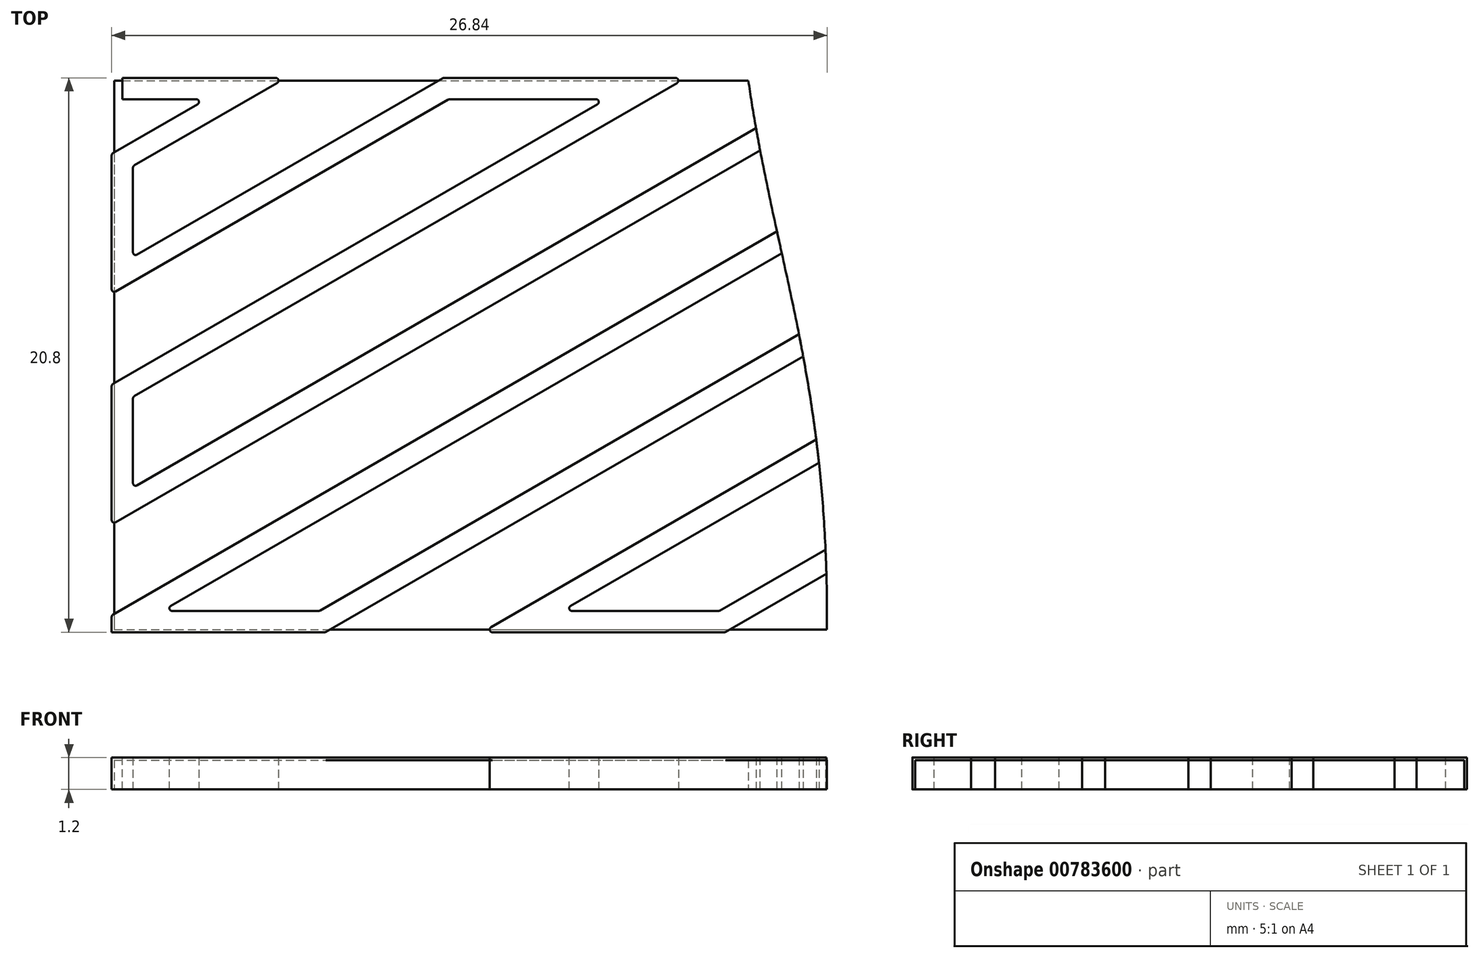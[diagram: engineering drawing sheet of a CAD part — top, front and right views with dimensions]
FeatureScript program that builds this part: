
annotation { "Feature Type Name" : "Feature", "Feature Type Description" : "" }
export const myFeature = defineFeature(function(context is Context, id is Id, definition is map)
    precondition{}
    {
        {
            var Q0;
            Q0=qCreatedBy(makeId("Top.planeOp"),FACE);
            var sketch = newSketch(context, id + "F0", { "sketchPlane" : qUnion([Q0])});
            skLineSegment(sketch, "E0.bottom", {"start": v(0, 0) * mm, "end": v(50, 0) * mm});
            skLineSegment(sketch, "E0.top", {"start": v(0, 20) * mm, "end": v(50, 20) * mm});
            skLineSegment(sketch, "E0.left", {"start": v(0, 0) * mm, "end": v(0, 20) * mm});
            skLineSegment(sketch, "E0.right", {"start": v(50, 0) * mm, "end": v(50, 20) * mm});
            skLineSegment(sketch, "E1", {"start": v(25, 36.98) * mm, "end": v(25, -17.72) * mm, "construction": true});
            skPoint(sketch, "E1.startSnap0", {"position": v(25, 20) * mm});
            skSolve(sketch);
        }
        {
            var Q0;
            Q0=sQuery(id+"F0.wireOp",EDGE,"E1");
            cPlane(context, id + "F1", {"entities" : qUnion([Q0]), "cplaneType" : CPlaneType.LINE_ANGLE, "offset" : 25 * mm, "angle" : 90 * degree, "width" : 150 * mm, "height" : 150 * mm});
        }
        {
            var Q0;
            Q0=qCreatedBy(makeId("Top.planeOp"),FACE);
            var sketch = newSketch(context, id + "F2", { "sketchPlane" : qUnion([Q0])});
            skLineSegment(sketch, "E2", {"start": v(0, 0) * mm, "end": v(34.64, 20) * mm});
            skLineSegment(sketch, "E3.1.0.0", {"start": v(7.5, 0) * mm, "end": v(42.14, 20) * mm});
            skLineSegment(sketch, "E3.2.0.0", {"start": v(15, 0) * mm, "end": v(49.64, 20) * mm});
            skLineSegment(sketch, "E3.3.0.0", {"start": v(22.5, 0) * mm, "end": v(50, 15.88) * mm});
            skLineSegment(sketch, "E3.4.0.0", {"start": v(30, 0) * mm, "end": v(50, 11.55) * mm});
            skLineSegment(sketch, "E3.5.0.0", {"start": v(37.5, 0) * mm, "end": v(50, 7.22) * mm});
            skLineSegment(sketch, "E3.6.0.0", {"start": v(45, 0) * mm, "end": v(50, 2.89) * mm});
            skLineSegment(sketch, "E4.1.0.0", {"start": v(0, 4.33) * mm, "end": v(27.14, 20) * mm});
            skLineSegment(sketch, "E4.2.0.0", {"start": v(0, 8.66) * mm, "end": v(19.64, 20) * mm});
            skLineSegment(sketch, "E4.3.0.0", {"start": v(0, 13) * mm, "end": v(12.14, 20) * mm});
            skLineSegment(sketch, "E4.4.0.0", {"start": v(0, 17.32) * mm, "end": v(4.64, 20) * mm});
            skLineSegment(sketch, "E5", {"start": v(0, 0) * mm, "end": v(7.5, 0) * mm});
            skLineSegment(sketch, "E6.1.0.0", {"start": v(15, 0) * mm, "end": v(22.5, 0) * mm});
            skLineSegment(sketch, "E6.2.0.0", {"start": v(30, 0) * mm, "end": v(37.5, 0) * mm});
            skLineSegment(sketch, "E6.3.0.0", {"start": v(45, 0) * mm, "end": v(50, 0) * mm});
            skLineSegment(sketch, "E7", {"start": v(0, 20) * mm, "end": v(4.64, 20) * mm});
            skLineSegment(sketch, "E8.1.0.0", {"start": v(12.14, 20) * mm, "end": v(19.64, 20) * mm});
            skLineSegment(sketch, "E8.2.0.0", {"start": v(27.14, 20) * mm, "end": v(34.64, 20) * mm});
            skLineSegment(sketch, "E8.3.0.0", {"start": v(42.14, 20) * mm, "end": v(49.64, 20) * mm});
            skPoint(sketch, "E9.orphan", {"position": v(-2.86, 20) * mm});
            skPoint(sketch, "E10.orphan", {"position": v(52.5, 0) * mm});
            skLineSegment(sketch, "E11", {"start": v(0, 4.33) * mm, "end": v(0, 8.66) * mm});
            skLineSegment(sketch, "E12", {"start": v(0, 13) * mm, "end": v(0, 17.32) * mm});
            skLineSegment(sketch, "E13", {"start": v(50, 15.88) * mm, "end": v(50, 11.55) * mm});
            skLineSegment(sketch, "E14", {"start": v(50, 7.22) * mm, "end": v(50, 2.89) * mm});
            skSolve(sketch);
        }
        {
            var Q0;
            Q0=sQuery(id+"F2.wireOp",VERTEX,"E7.start");
            var Q1;
            Q1=sQuery(id+"F2.wireOp",EDGE,"E7");
            cPlane(context, id + "F3", {"entities" : qUnion([Q0, Q1]), "cplaneType" : CPlaneType.LINE_POINT, "offset" : 25 * mm, "width" : 150 * mm, "height" : 150 * mm});
        }
        {
            var Q0;
            Q0=qCreatedBy(id+"F3.planeOp",FACE);
            var sketch = newSketch(context, id + "F4", { "sketchPlane" : qUnion([Q0])});
            skPoint(sketch, "E15.0", {"position": v(20, 0) * mm});
            skLineSegment(sketch, "E16", {"start": v(20, 0) * mm, "end": v(20.4, 0) * mm});
            skLineSegment(sketch, "E17", {"start": v(20.4, 0) * mm, "end": v(20.4, 1.2) * mm});
            skLineSegment(sketch, "E18", {"start": v(20.4, 1.2) * mm, "end": v(20, 1.2) * mm});
            skLineSegment(sketch, "E19", {"start": v(20, -0.76) * mm, "end": v(20, 2.5) * mm, "construction": true});
            skLineSegment(sketch, "E20.MirrorCS", {"start": v(19.6, 1.2) * mm, "end": v(20, 1.2) * mm});
            skLineSegment(sketch, "E21.MirrorCS", {"start": v(20, 0) * mm, "end": v(19.6, 0) * mm});
            skLineSegment(sketch, "E22.MirrorCS", {"start": v(19.6, 0) * mm, "end": v(19.6, 1.2) * mm});
            skSolve(sketch);
        }
        {
            var Q0;
            Q0=qSketchRegion(id+"F4",true);
            var Q1;
            Q1=sQuery(id+"F2.wireOp",EDGE,"E7");
            var Q2;
            Q2=sQuery(id+"F2.wireOp",EDGE,"E4.4.0.0");
            var Q3;
            Q3=sQuery(id+"F2.wireOp",EDGE,"E12");
            var Q4;
            Q4=sQuery(id+"F2.wireOp",EDGE,"E4.3.0.0");
            var Q5;
            Q5=sQuery(id+"F2.wireOp",EDGE,"E8.1.0.0");
            var Q6;
            Q6=sQuery(id+"F2.wireOp",EDGE,"E4.2.0.0");
            var Q7;
            Q7=sQuery(id+"F2.wireOp",EDGE,"E11");
            var Q8;
            Q8=sQuery(id+"F2.wireOp",EDGE,"E4.1.0.0");
            var Q9;
            Q9=sQuery(id+"F2.wireOp",EDGE,"E8.2.0.0");
            var Q10;
            Q10=sQuery(id+"F2.wireOp",EDGE,"E2");
            var Q11;
            Q11=sQuery(id+"F2.wireOp",EDGE,"E5");
            var Q12;
            Q12=sQuery(id+"F2.wireOp",EDGE,"E3.1.0.0");
            var Q13;
            Q13=sQuery(id+"F2.wireOp",EDGE,"E3.2.0.0");
            var Q14;
            Q14=sQuery(id+"F2.wireOp",EDGE,"E8.3.0.0");
            var Q15;
            Q15=sQuery(id+"F2.wireOp",EDGE,"E6.1.0.0");
            var Q16;
            Q16=sQuery(id+"F2.wireOp",EDGE,"E3.3.0.0");
            var Q17;
            Q17=sQuery(id+"F2.wireOp",EDGE,"E13");
            var Q18;
            Q18=sQuery(id+"F2.wireOp",EDGE,"E3.4.0.0");
            var Q19;
            Q19=sQuery(id+"F2.wireOp",EDGE,"E6.2.0.0");
            var Q20;
            Q20=sQuery(id+"F2.wireOp",EDGE,"E3.5.0.0");
            var Q21;
            Q21=sQuery(id+"F2.wireOp",EDGE,"E14");
            var Q22;
            Q22=sQuery(id+"F2.wireOp",EDGE,"E3.6.0.0");
            var Q23;
            Q23=sQuery(id+"F2.wireOp",EDGE,"E6.3.0.0");
            sweep(context, id + "F5", {"profiles" : qUnion([Q0]), "path" : qUnion([Q1, Q2, Q3, Q4, Q5, Q6, Q7, Q8, Q9, Q10, Q11, Q12, Q13, Q14, Q15, Q16, Q17, Q18, Q19, Q20, Q21, Q22, Q23])});
        }
        {
            var Q0;
            Q0=qCreatedBy(makeId("Top.planeOp"),FACE);
            var sketch = newSketch(context, id + "F6", { "sketchPlane" : qUnion([Q0])});
            skLineSegment(sketch, "E23.0", {"start": v(-0.4, 8.9) * mm, "end": v(-0.4, 3.64) * mm});
            skLineSegment(sketch, "E24.0", {"start": v(0, 20.4) * mm, "end": v(6.13, 20.4) * mm});
            skLineSegment(sketch, "E25.0", {"start": v(28.5, -0.4) * mm, "end": v(37.6, -0.4) * mm});
            skLineSegment(sketch, "E26.0", {"start": v(50.4, 16.57) * mm, "end": v(50.4, 11.32) * mm});
            skLineSegment(sketch, "E27.bottom", {"start": v(-0.4, 20.4) * mm, "end": v(50.4, 20.4) * mm});
            skLineSegment(sketch, "E27.top", {"start": v(-0.4, -0.4) * mm, "end": v(50.4, -0.4) * mm});
            skLineSegment(sketch, "E27.left", {"start": v(-0.4, 20.4) * mm, "end": v(-0.4, -0.4) * mm});
            skLineSegment(sketch, "E27.right", {"start": v(50.4, 20.4) * mm, "end": v(50.4, -0.4) * mm});
            skLineSegment(sketch, "E28.bottom", {"start": v(-6.4, 28.18) * mm, "end": v(56.43, 28.18) * mm});
            skLineSegment(sketch, "E28.top", {"start": v(-6.4, -9.1) * mm, "end": v(56.43, -9.1) * mm});
            skLineSegment(sketch, "E28.left", {"start": v(-6.4, 28.18) * mm, "end": v(-6.4, -9.1) * mm});
            skLineSegment(sketch, "E28.right", {"start": v(56.43, 28.18) * mm, "end": v(56.43, -9.1) * mm});
            skSolve(sketch);
        }
        {
            var Q0;
            {var subQ1=sQuery(id+"F6.wireOp",EDGE,"E23.0");Q0=makeQuery(id+"F6.imprint","IMPRINT",FACE,{"disambiguationData":[TD([[makeQuery(id+"F6.imprint","IMPRINT",EDGE,{"derivedFrom":subQ1}),-1.0]])]});}
            extrude(context, id + "F7", {"entities" : qUnion([Q0]), "depth" : 25 * mm, "offsetDistance" : 25 * mm});
        }
        {
            var Q0;
            Q0=makeQuery(id+"F7.opExtrude","SWEPT_BODY",BODY,{"disambiguationData":[OSD([sQuery(id+"F6.wireOp",EDGE,"E23.0"),sQuery(id+"F6.wireOp",EDGE,"E24.0"),sQuery(id+"F6.wireOp",EDGE,"E25.0"),sQuery(id+"F6.wireOp",EDGE,"E26.0"),sQuery(id+"F6.wireOp",EDGE,"E27.bottom"),sQuery(id+"F6.wireOp",EDGE,"E27.top"),sQuery(id+"F6.wireOp",EDGE,"E27.left"),sQuery(id+"F6.wireOp",EDGE,"E27.right"),sQuery(id+"F6.wireOp",EDGE,"E28.bottom"),sQuery(id+"F6.wireOp",EDGE,"E28.top"),sQuery(id+"F6.wireOp",EDGE,"E28.left"),sQuery(id+"F6.wireOp",EDGE,"E28.right")])]});
            var Q1;
            Q1=makeQuery(id+"F5.opSweep","SWEPT_BODY",BODY,{"disambiguationData":[OSD([sQuery(id+"F2.wireOp",EDGE,"E3.1.0.0"),sQuery(id+"F4.wireOp",EDGE,"E16"),sQuery(id+"F4.wireOp",EDGE,"E17"),sQuery(id+"F4.wireOp",EDGE,"E18"),sQuery(id+"F4.wireOp",EDGE,"E20.MirrorCS"),sQuery(id+"F4.wireOp",EDGE,"E21.MirrorCS"),sQuery(id+"F4.wireOp",EDGE,"E22.MirrorCS")])]});
            booleanBodies(context, id + "F8", {"operationType" : BooleanOperationType.SUBTRACTION, "tools" : qUnion([Q0]), "targets" : qUnion([Q1])});
        }
        {
            var Q0;
            Q0=qCreatedBy(makeId("Top.planeOp"),FACE);
            var sketch = newSketch(context, id + "F9", { "sketchPlane" : qUnion([Q0])});
            skLineSegment(sketch, "E29.0", {"start": v(-0.3, 20.3) * mm, "end": v(50.3, 20.3) * mm});
            skLineSegment(sketch, "E29.1", {"start": v(-0.3, 20.3) * mm, "end": v(-0.3, -0.3) * mm});
            skLineSegment(sketch, "E29.2", {"start": v(-0.3, -0.3) * mm, "end": v(50.3, -0.3) * mm});
            skLineSegment(sketch, "E29.3", {"start": v(50.3, 20.3) * mm, "end": v(50.3, -0.3) * mm});
            skSolve(sketch);
        }
        {
            var Q0;
            Q0=qSketchRegion(id+"F9",true);
            extrude(context, id + "F10", {"entities" : qUnion([Q0]), "depth" : 1.1 * mm, "offsetDistance" : 25 * mm});
        }
        {
            var Q0;
            Q0=makeQuery(id+"F5.opSweep","MID_CAP_EDGE",EDGE,{"disambiguationData":[OSD([sQuery(id+"F2.wireOp",VERTEX,"E12.end"),sQuery(id+"F4.wireOp",EDGE,"E22.MirrorCS")])],"capPos":2.0});
            var Q1;
            Q1=makeQuery(id+"F5.opSweep","MID_CAP_EDGE",EDGE,{"disambiguationData":[OSD([sQuery(id+"F2.wireOp",VERTEX,"E4.4.0.0.end"),sQuery(id+"F4.wireOp",EDGE,"E22.MirrorCS")])],"capPos":1.0});
            var Q2;
            Q2=makeQuery(id+"F5.opSweep","MID_CAP_EDGE",EDGE,{"disambiguationData":[OSD([sQuery(id+"F2.wireOp",VERTEX,"E4.4.0.0.end"),sQuery(id+"F4.wireOp",EDGE,"E17")])],"capPos":1.0});
            var Q3;
            Q3=makeQuery(id+"F5.opSweep","MID_CAP_EDGE",EDGE,{"disambiguationData":[OSD([sQuery(id+"F2.wireOp",VERTEX,"E12.end"),sQuery(id+"F4.wireOp",EDGE,"E17")])],"capPos":2.0});
            var Q4;
            Q4=makeQuery(id+"F5.opSweep","MID_CAP_EDGE",EDGE,{"disambiguationData":[OSD([sQuery(id+"F2.wireOp",VERTEX,"E4.3.0.0.start"),sQuery(id+"F4.wireOp",EDGE,"E17")])],"capPos":3.0});
            var Q5;
            Q5=makeQuery(id+"F5.opSweep","MID_CAP_EDGE",EDGE,{"disambiguationData":[OSD([sQuery(id+"F2.wireOp",VERTEX,"E4.3.0.0.start"),sQuery(id+"F4.wireOp",EDGE,"E22.MirrorCS")])],"capPos":3.0});
            var Q6;
            Q6=makeQuery(id+"F5.opSweep","MID_CAP_EDGE",EDGE,{"disambiguationData":[OSD([sQuery(id+"F2.wireOp",VERTEX,"E8.1.0.0.start"),sQuery(id+"F4.wireOp",EDGE,"E22.MirrorCS")])],"capPos":4.0});
            var Q7;
            Q7=makeQuery(id+"F5.opSweep","MID_CAP_EDGE",EDGE,{"disambiguationData":[OSD([sQuery(id+"F2.wireOp",VERTEX,"E8.1.0.0.start"),sQuery(id+"F4.wireOp",EDGE,"E17")])],"capPos":4.0});
            var Q8;
            Q8=makeQuery(id+"F5.opSweep","MID_CAP_EDGE",EDGE,{"disambiguationData":[OSD([sQuery(id+"F2.wireOp",VERTEX,"E4.2.0.0.end"),sQuery(id+"F4.wireOp",EDGE,"E22.MirrorCS")])],"capPos":5.0});
            var Q9;
            Q9=makeQuery(id+"F5.opSweep","MID_CAP_EDGE",EDGE,{"disambiguationData":[OSD([sQuery(id+"F2.wireOp",VERTEX,"E4.2.0.0.end"),sQuery(id+"F4.wireOp",EDGE,"E17")])],"capPos":5.0});
            var Q10;
            Q10=makeQuery(id+"F5.opSweep","MID_CAP_EDGE",EDGE,{"disambiguationData":[OSD([sQuery(id+"F2.wireOp",VERTEX,"E8.2.0.0.start"),sQuery(id+"F4.wireOp",EDGE,"E17")])],"capPos":8.0});
            var Q11;
            Q11=makeQuery(id+"F5.opSweep","MID_CAP_EDGE",EDGE,{"disambiguationData":[OSD([sQuery(id+"F2.wireOp",VERTEX,"E11.end"),sQuery(id+"F4.wireOp",EDGE,"E22.MirrorCS")])],"capPos":6.0});
            var Q12;
            Q12=makeQuery(id+"F5.opSweep","MID_CAP_EDGE",EDGE,{"disambiguationData":[OSD([sQuery(id+"F2.wireOp",VERTEX,"E11.end"),sQuery(id+"F4.wireOp",EDGE,"E17")])],"capPos":6.0});
            var Q13;
            Q13=makeQuery(id+"F5.opSweep","MID_CAP_EDGE",EDGE,{"disambiguationData":[OSD([sQuery(id+"F2.wireOp",VERTEX,"E4.1.0.0.start"),sQuery(id+"F4.wireOp",EDGE,"E17")])],"capPos":7.0});
            var Q14;
            Q14=makeQuery(id+"F5.opSweep","MID_CAP_EDGE",EDGE,{"disambiguationData":[OSD([sQuery(id+"F2.wireOp",VERTEX,"E4.1.0.0.start"),sQuery(id+"F4.wireOp",EDGE,"E22.MirrorCS")])],"capPos":7.0});
            var Q15;
            Q15=makeQuery(id+"F5.opSweep","MID_CAP_EDGE",EDGE,{"disambiguationData":[OSD([sQuery(id+"F2.wireOp",VERTEX,"E8.2.0.0.start"),sQuery(id+"F4.wireOp",EDGE,"E22.MirrorCS")])],"capPos":8.0});
            var Q16;
            Q16=makeQuery(id+"F5.opSweep","MID_CAP_EDGE",EDGE,{"disambiguationData":[OSD([sQuery(id+"F2.wireOp",VERTEX,"E2.end"),sQuery(id+"F4.wireOp",EDGE,"E22.MirrorCS")])],"capPos":9.0});
            var Q17;
            Q17=makeQuery(id+"F5.opSweep","MID_CAP_EDGE",EDGE,{"disambiguationData":[OSD([sQuery(id+"F2.wireOp",VERTEX,"E2.end"),sQuery(id+"F4.wireOp",EDGE,"E17")])],"capPos":9.0});
            var Q18;
            Q18=makeQuery(id+"F5.opSweep","MID_CAP_EDGE",EDGE,{"disambiguationData":[OSD([sQuery(id+"F2.wireOp",VERTEX,"E8.3.0.0.start"),sQuery(id+"F4.wireOp",EDGE,"E17")])],"capPos":12.0});
            var Q19;
            Q19=makeQuery(id+"F8.opBoolean","INTERSECT",EDGE,{"derivedFrom":[makeQuery(id+"F5.opSweep","SWEPT_FACE",FACE,{"disambiguationData":[OSD([sQuery(id+"F2.wireOp",EDGE,"E2"),sQuery(id+"F4.wireOp",EDGE,"E22.MirrorCS")])]}),makeQuery(id+"F7.opExtrude","SWEPT_FACE",FACE,{"disambiguationData":[OSD([sQuery(id+"F6.wireOp",EDGE,"E23.0"),sQuery(id+"F6.wireOp",EDGE,"E27.left")])]})]});
            var Q20;
            Q20=makeQuery(id+"F5.opSweep","MID_CAP_EDGE",EDGE,{"disambiguationData":[OSD([sQuery(id+"F2.wireOp",VERTEX,"E5.start"),sQuery(id+"F4.wireOp",EDGE,"E17")])],"capPos":10.0});
            var Q21;
            Q21=makeQuery(id+"F8.opBoolean","COPY",EDGE,{"derivedFrom":makeQuery(id+"F7.opExtrude","SWEPT_EDGE",EDGE,{"disambiguationData":[OSD([sQuery(id+"F6.wireOp",EDGE,"E27.top"),sQuery(id+"F6.wireOp",EDGE,"E27.left")])]})});
            var Q22;
            Q22=makeQuery(id+"F5.opSweep","MID_CAP_EDGE",EDGE,{"disambiguationData":[OSD([sQuery(id+"F2.wireOp",VERTEX,"E3.1.0.0.start"),sQuery(id+"F4.wireOp",EDGE,"E17")])],"capPos":11.0});
            var Q23;
            Q23=makeQuery(id+"F5.opSweep","MID_CAP_EDGE",EDGE,{"disambiguationData":[OSD([sQuery(id+"F2.wireOp",VERTEX,"E3.1.0.0.start"),sQuery(id+"F4.wireOp",EDGE,"E22.MirrorCS")])],"capPos":11.0});
            var Q24;
            Q24=makeQuery(id+"F5.opSweep","MID_CAP_EDGE",EDGE,{"disambiguationData":[OSD([sQuery(id+"F2.wireOp",VERTEX,"E8.3.0.0.start"),sQuery(id+"F4.wireOp",EDGE,"E22.MirrorCS")])],"capPos":12.0});
            var Q25;
            Q25=makeQuery(id+"F5.opSweep","MID_CAP_EDGE",EDGE,{"disambiguationData":[OSD([sQuery(id+"F2.wireOp",VERTEX,"E8.3.0.0.end"),sQuery(id+"F4.wireOp",EDGE,"E22.MirrorCS")])],"capPos":13.0});
            var Q26;
            Q26=makeQuery(id+"F8.opBoolean","COPY",EDGE,{"derivedFrom":makeQuery(id+"F7.opExtrude","SWEPT_EDGE",EDGE,{"disambiguationData":[OSD([sQuery(id+"F6.wireOp",EDGE,"E27.bottom"),sQuery(id+"F6.wireOp",EDGE,"E27.right")])]})});
            var Q27;
            Q27=makeQuery(id+"F8.opBoolean","INTERSECT",EDGE,{"derivedFrom":[makeQuery(id+"F5.opSweep","SWEPT_FACE",FACE,{"disambiguationData":[OSD([sQuery(id+"F2.wireOp",EDGE,"E3.2.0.0"),sQuery(id+"F4.wireOp",EDGE,"E17")])]}),makeQuery(id+"F7.opExtrude","SWEPT_FACE",FACE,{"disambiguationData":[OSD([sQuery(id+"F6.wireOp",EDGE,"E26.0"),sQuery(id+"F6.wireOp",EDGE,"E27.right")])]})]});
            var Q28;
            Q28=makeQuery(id+"F5.opSweep","MID_CAP_EDGE",EDGE,{"disambiguationData":[OSD([sQuery(id+"F2.wireOp",VERTEX,"E13.start"),sQuery(id+"F4.wireOp",EDGE,"E17")])],"capPos":16.0});
            var Q29;
            Q29=makeQuery(id+"F5.opSweep","MID_CAP_EDGE",EDGE,{"disambiguationData":[OSD([sQuery(id+"F2.wireOp",VERTEX,"E13.start"),sQuery(id+"F4.wireOp",EDGE,"E22.MirrorCS")])],"capPos":16.0});
            var Q30;
            Q30=makeQuery(id+"F5.opSweep","MID_CAP_EDGE",EDGE,{"disambiguationData":[OSD([sQuery(id+"F2.wireOp",VERTEX,"E3.4.0.0.end"),sQuery(id+"F4.wireOp",EDGE,"E22.MirrorCS")])],"capPos":17.0});
            var Q31;
            Q31=makeQuery(id+"F5.opSweep","MID_CAP_EDGE",EDGE,{"disambiguationData":[OSD([sQuery(id+"F2.wireOp",VERTEX,"E3.4.0.0.end"),sQuery(id+"F4.wireOp",EDGE,"E17")])],"capPos":17.0});
            var Q32;
            Q32=makeQuery(id+"F5.opSweep","MID_CAP_EDGE",EDGE,{"disambiguationData":[OSD([sQuery(id+"F2.wireOp",VERTEX,"E6.2.0.0.start"),sQuery(id+"F4.wireOp",EDGE,"E22.MirrorCS")])],"capPos":18.0});
            var Q33;
            Q33=makeQuery(id+"F5.opSweep","MID_CAP_EDGE",EDGE,{"disambiguationData":[OSD([sQuery(id+"F2.wireOp",VERTEX,"E6.2.0.0.start"),sQuery(id+"F4.wireOp",EDGE,"E17")])],"capPos":18.0});
            var Q34;
            Q34=makeQuery(id+"F5.opSweep","MID_CAP_EDGE",EDGE,{"disambiguationData":[OSD([sQuery(id+"F2.wireOp",VERTEX,"E3.3.0.0.start"),sQuery(id+"F4.wireOp",EDGE,"E22.MirrorCS")])],"capPos":15.0});
            var Q35;
            Q35=makeQuery(id+"F5.opSweep","MID_CAP_EDGE",EDGE,{"disambiguationData":[OSD([sQuery(id+"F2.wireOp",VERTEX,"E6.1.0.0.start"),sQuery(id+"F4.wireOp",EDGE,"E22.MirrorCS")])],"capPos":14.0});
            var Q36;
            Q36=makeQuery(id+"F5.opSweep","MID_CAP_EDGE",EDGE,{"disambiguationData":[OSD([sQuery(id+"F2.wireOp",VERTEX,"E6.1.0.0.start"),sQuery(id+"F4.wireOp",EDGE,"E17")])],"capPos":14.0});
            var Q37;
            Q37=makeQuery(id+"F5.opSweep","MID_CAP_EDGE",EDGE,{"disambiguationData":[OSD([sQuery(id+"F2.wireOp",VERTEX,"E3.5.0.0.start"),sQuery(id+"F4.wireOp",EDGE,"E17")])],"capPos":19.0});
            var Q38;
            Q38=makeQuery(id+"F5.opSweep","MID_CAP_EDGE",EDGE,{"disambiguationData":[OSD([sQuery(id+"F2.wireOp",VERTEX,"E3.3.0.0.start"),sQuery(id+"F4.wireOp",EDGE,"E17")])],"capPos":15.0});
            var Q39;
            Q39=makeQuery(id+"F5.opSweep","MID_CAP_EDGE",EDGE,{"disambiguationData":[OSD([sQuery(id+"F2.wireOp",VERTEX,"E14.start"),sQuery(id+"F4.wireOp",EDGE,"E17")])],"capPos":20.0});
            var Q40;
            Q40=makeQuery(id+"F5.opSweep","MID_CAP_EDGE",EDGE,{"disambiguationData":[OSD([sQuery(id+"F2.wireOp",VERTEX,"E14.start"),sQuery(id+"F4.wireOp",EDGE,"E22.MirrorCS")])],"capPos":20.0});
            var Q41;
            Q41=makeQuery(id+"F5.opSweep","MID_CAP_EDGE",EDGE,{"disambiguationData":[OSD([sQuery(id+"F2.wireOp",VERTEX,"E3.5.0.0.start"),sQuery(id+"F4.wireOp",EDGE,"E22.MirrorCS")])],"capPos":19.0});
            var Q42;
            Q42=makeQuery(id+"F5.opSweep","MID_CAP_EDGE",EDGE,{"disambiguationData":[OSD([sQuery(id+"F2.wireOp",VERTEX,"E6.3.0.0.start"),sQuery(id+"F4.wireOp",EDGE,"E22.MirrorCS")])],"capPos":22.0});
            var Q43;
            Q43=makeQuery(id+"F5.opSweep","MID_CAP_EDGE",EDGE,{"disambiguationData":[OSD([sQuery(id+"F2.wireOp",VERTEX,"E3.6.0.0.end"),sQuery(id+"F4.wireOp",EDGE,"E17")])],"capPos":21.0});
            var Q44;
            Q44=makeQuery(id+"F5.opSweep","MID_CAP_EDGE",EDGE,{"disambiguationData":[OSD([sQuery(id+"F2.wireOp",VERTEX,"E6.3.0.0.start"),sQuery(id+"F4.wireOp",EDGE,"E17")])],"capPos":22.0});
            var Q45;
            Q45=makeQuery(id+"F5.opSweep","MID_CAP_EDGE",EDGE,{"disambiguationData":[OSD([sQuery(id+"F2.wireOp",VERTEX,"E3.6.0.0.end"),sQuery(id+"F4.wireOp",EDGE,"E22.MirrorCS")])],"capPos":21.0});
            fillet(context, id + "F11", {"entities" : qUnion([Q0, Q1, Q2, Q3, Q4, Q5, Q6, Q7, Q8, Q9, Q10, Q11, Q12, Q13, Q14, Q15, Q16, Q17, Q18, Q19, Q20, Q21, Q22, Q23, Q24, Q25, Q26, Q27, Q28, Q29, Q30, Q31, Q32, Q33, Q34, Q35, Q36, Q37, Q38, Q39, Q40, Q41, Q42, Q43, Q44, Q45]), "radius" : .1 * mm, "tangentPropagation" : true, "allowEdgeOverflow" : false});
        }
        {
            var Q0;
            Q0=qCreatedBy(makeId("Top.planeOp"),FACE);
            var sketch = newSketch(context, id + "F12", { "sketchPlane" : qUnion([Q0])});
            skLineSegment(sketch, "E30.0", {"start": v(42.06, 20.4) * mm, "end": v(50.3, 20.4) * mm});
            skLineSegment(sketch, "E31.0", {"start": v(50.4, 16.4) * mm, "end": v(50.4, 11.37) * mm});
            skLineSegment(sketch, "E32.0", {"start": v(43.88, -0.4) * mm, "end": v(50, -0.4) * mm});
            skLineSegment(sketch, "E33.bottom", {"start": v(50.4, 20.4) * mm, "end": v(33.26, 20.4) * mm});
            skLineSegment(sketch, "E33.top", {"start": v(50.4, -0.4) * mm, "end": v(33.26, -0.4) * mm});
            skLineSegment(sketch, "E33.left", {"start": v(50.4, 20.4) * mm, "end": v(50.4, -0.4) * mm});
            skLineSegment(sketch, "E34", {"start": v(33.26, 20.4) * mm, "end": v(23.47, 20.4) * mm});
            skLineSegment(sketch, "E35", {"start": v(23.47, -0.4) * mm, "end": v(41.24, -0.4) * mm});
            skFitSpline(sketch, "E36", {"points": [v(23.47, 20.4) * mm, v(26.43, -0.4) * mm], "startDerivative": vector(2.96, -20.8) * mm, "endDerivative": vector(-0.26, -28.2) * mm});
            skSolve(sketch);
        }
        {
            var Q0;
            Q0=qSketchRegion(id+"F12",true);
            extrude(context, id + "F13", {"entities" : qUnion([Q0]), "depth" : 25 * mm, "offsetDistance" : 25 * mm});
        }
        {
            var Q0;
            Q0=makeQuery(id+"F13.opExtrude","SWEPT_BODY",BODY,{"disambiguationData":[OSD([sQuery(id+"F12.wireOp",EDGE,"E33.bottom"),sQuery(id+"F12.wireOp",EDGE,"E33.top"),sQuery(id+"F12.wireOp",EDGE,"E33.left"),sQuery(id+"F12.wireOp",EDGE,"d843b8a2-55aa-41e5-a9ed-f4f07de17de5")])]});
            var Q1;
            Q1=makeQuery(id+"F10.opExtrude","SWEPT_BODY",BODY,{"disambiguationData":[OSD([sQuery(id+"F9.wireOp",EDGE,"E29.0"),sQuery(id+"F9.wireOp",EDGE,"E29.1"),sQuery(id+"F9.wireOp",EDGE,"E29.2"),sQuery(id+"F9.wireOp",EDGE,"E29.3")])]});
            var Q2;
            Q2=makeQuery(id+"F5.opSweep","SWEPT_BODY",BODY,{"disambiguationData":[OSD([sQuery(id+"F2.wireOp",EDGE,"E3.1.0.0"),sQuery(id+"F4.wireOp",EDGE,"E16"),sQuery(id+"F4.wireOp",EDGE,"E17"),sQuery(id+"F4.wireOp",EDGE,"E18"),sQuery(id+"F4.wireOp",EDGE,"E20.MirrorCS"),sQuery(id+"F4.wireOp",EDGE,"E21.MirrorCS"),sQuery(id+"F4.wireOp",EDGE,"E22.MirrorCS")])]});
            booleanBodies(context, id + "F14", {"operationType" : BooleanOperationType.SUBTRACTION, "tools" : qUnion([Q0]), "targets" : qUnion([Q1, Q2])});
        }
    });
